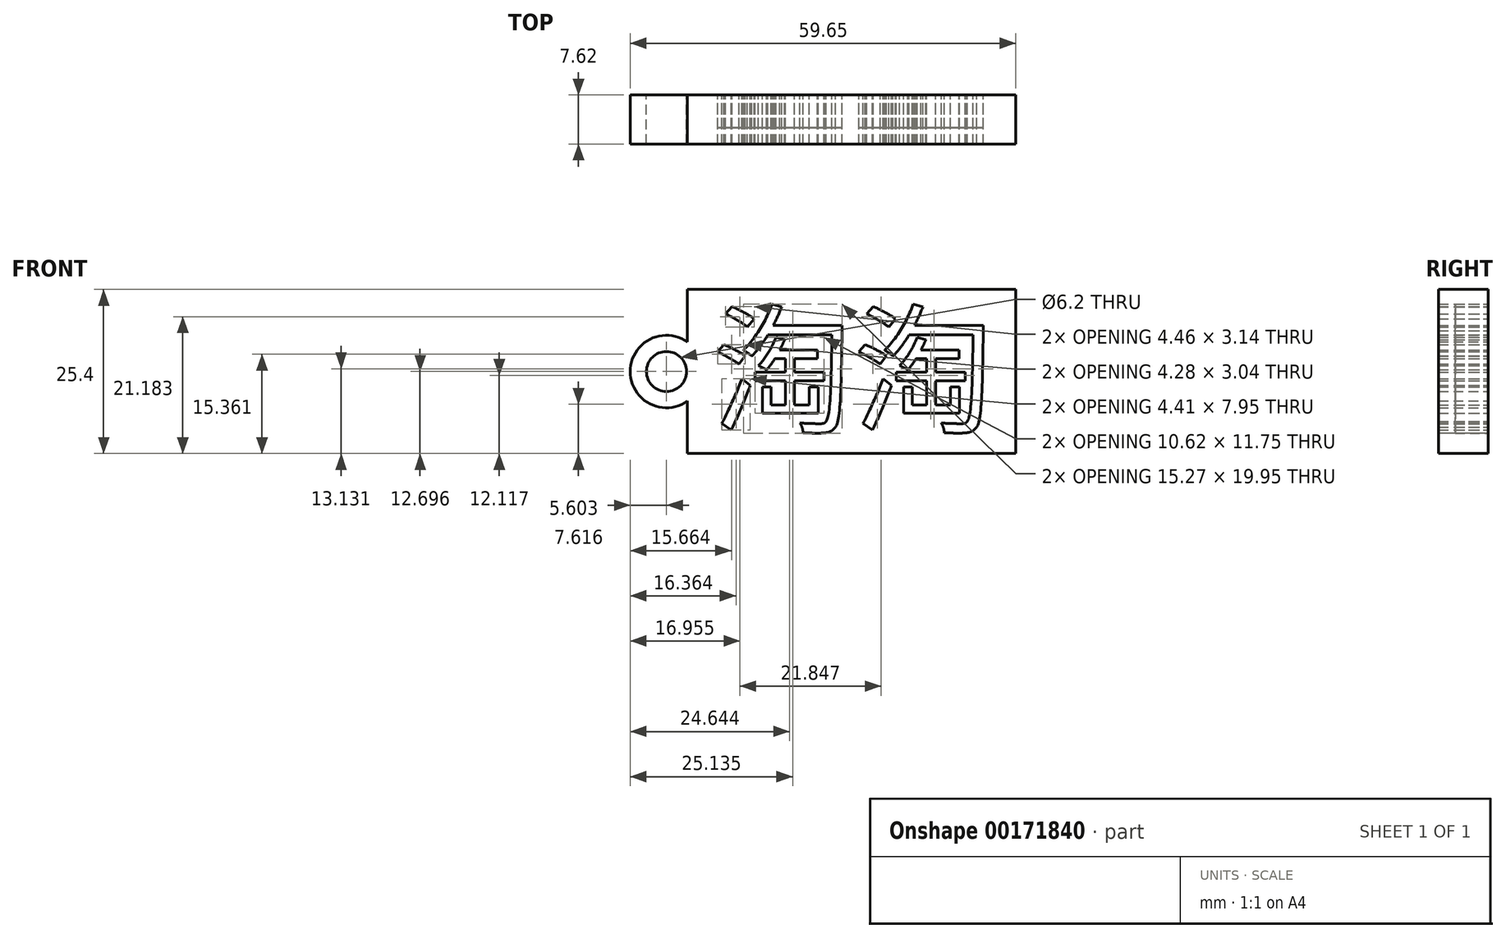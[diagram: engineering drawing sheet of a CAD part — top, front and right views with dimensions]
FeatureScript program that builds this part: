
annotation { "Feature Type Name" : "Feature", "Feature Type Description" : "" }
export const myFeature = defineFeature(function(context is Context, id is Id, definition is map)
    precondition{}
    {
        {
            var Q0;
            Q0=qCreatedBy(makeId("Front.planeOp"),FACE);
            var sketch = newSketch(context, id + "F0", { "sketchPlane" : qUnion([Q0])});
            skLineSegment(sketch, "E0.bottom", {"start": v(-20.3, 9.94) * mm, "end": v(30.5, 9.94) * mm});
            skLineSegment(sketch, "E0.top", {"start": v(-20.3, -15.46) * mm, "end": v(30.5, -15.46) * mm});
            skLineSegment(sketch, "E0.left", {"start": v(-20.3, 9.94) * mm, "end": v(-20.3, -15.46) * mm});
            skLineSegment(sketch, "E0.right", {"start": v(30.5, 9.94) * mm, "end": v(30.5, -15.46) * mm});
            skText(sketch, "E1", { "text": "淘淘", "fontName": "NotoSansCJKsc-Regular.otf"});
            skArc(sketch, "E2", {"start": v(-20.3, 1.8) * mm, "mid": v(-29.15, -2.76) * mm, "end": v(-20.3, -7.34) * mm});
            skCircle(sketch, "E3", {"center": v(-23.55, -2.76) * mm, "radius": 3.1 * mm});
            const initialGuessF0  = {"E1": [-0.0165, -0.01064, 1, 0, 0.01573]};
            skSetInitialGuess(sketch, initialGuessF0);
            skSolve(sketch);
        }
        {
            var Q0;
            Q0=makeQuery(id+"F0.imprint","IMPRINT",FACE,{"disambiguationData":[TD([[makeQuery(id+"F0.imprint","IMPRINT",EDGE,{"derivedFrom":sQuery(id+"F0.wireOp",EDGE,"E1.sketch_text.stroke-40")}),1.0]])]});
            var Q1;
            Q1=makeQuery(id+"F0.imprint","IMPRINT",FACE,{"disambiguationData":[TD([[makeQuery(id+"F0.imprint","IMPRINT",EDGE,{"derivedFrom":sQuery(id+"F0.wireOp",EDGE,"E1.sketch_text.stroke-0")}),1.0]])]});
            var Q2;
            Q2=makeQuery(id+"F0.imprint","IMPRINT",FACE,{"disambiguationData":[TD([[makeQuery(id+"F0.imprint","IMPRINT",EDGE,{"derivedFrom":sQuery(id+"F0.wireOp",EDGE,"E1.sketch_text.stroke-4")}),1.0]])]});
            var Q3;
            Q3=makeQuery(id+"F0.imprint","IMPRINT",FACE,{"disambiguationData":[TD([[makeQuery(id+"F0.imprint","IMPRINT",EDGE,{"derivedFrom":sQuery(id+"F0.wireOp",EDGE,"E1.sketch_text.stroke-8")}),1.0]])]});
            var Q4;
            Q4=makeQuery(id+"F0.imprint","IMPRINT",FACE,{"disambiguationData":[TD([[makeQuery(id+"F0.imprint","IMPRINT",EDGE,{"derivedFrom":sQuery(id+"F0.wireOp",EDGE,"E1.sketch_text.stroke-12")}),1.0]])]});
            var Q5;
            Q5=makeQuery(id+"F0.imprint","IMPRINT",FACE,{"disambiguationData":[TD([[makeQuery(id+"F0.imprint","IMPRINT",EDGE,{"derivedFrom":sQuery(id+"F0.wireOp",EDGE,"E1.sketch_text.stroke-59")}),1.0]])]});
            var Q6;
            Q6=makeQuery(id+"F0.imprint","IMPRINT",FACE,{"disambiguationData":[TD([[makeQuery(id+"F0.imprint","IMPRINT",EDGE,{"derivedFrom":sQuery(id+"F0.wireOp",EDGE,"E1.sketch_text.stroke-95")}),1.0]])]});
            var Q7;
            Q7=makeQuery(id+"F0.imprint","IMPRINT",FACE,{"disambiguationData":[TD([[makeQuery(id+"F0.imprint","IMPRINT",EDGE,{"derivedFrom":sQuery(id+"F0.wireOp",EDGE,"E1.sketch_text.stroke-55")}),1.0]])]});
            var Q8;
            Q8=makeQuery(id+"F0.imprint","IMPRINT",FACE,{"disambiguationData":[TD([[makeQuery(id+"F0.imprint","IMPRINT",EDGE,{"derivedFrom":sQuery(id+"F0.wireOp",EDGE,"E1.sketch_text.stroke-67")}),1.0]])]});
            var Q9;
            Q9=makeQuery(id+"F0.imprint","IMPRINT",FACE,{"disambiguationData":[TD([[makeQuery(id+"F0.imprint","IMPRINT",EDGE,{"derivedFrom":sQuery(id+"F0.wireOp",EDGE,"E1.sketch_text.stroke-63")}),1.0]])]});
            extrude(context, id + "F1", {"entities" : qUnion([Q0, Q1, Q2, Q3, Q4, Q5, Q6, Q7, Q8, Q9]), "depth" : 5.08 * mm});
        }
        {
            var Q0;
            Q0=makeQuery(id+"F0.imprint","IMPRINT",FACE,{"disambiguationData":[TD([[makeQuery(id+"F0.imprint","IMPRINT",EDGE,{"derivedFrom":sQuery(id+"F0.wireOp",EDGE,"E0.bottom")}),-1.0]])]});
            var Q1;
            {var subQ0=sQuery(id+"F0.wireOp",EDGE,"E2");Q1=makeQuery(id+"F0.imprint","IMPRINT",FACE,{"disambiguationData":[TD([[makeQuery(id+"F0.imprint","IMPRINT",EDGE,{"derivedFrom":subQ0}),1.0]])]});}
            extrude(context, id + "F2", {"entities" : qUnion([Q0, Q1]), "depth" : 7.62 * mm});
        }
    });
